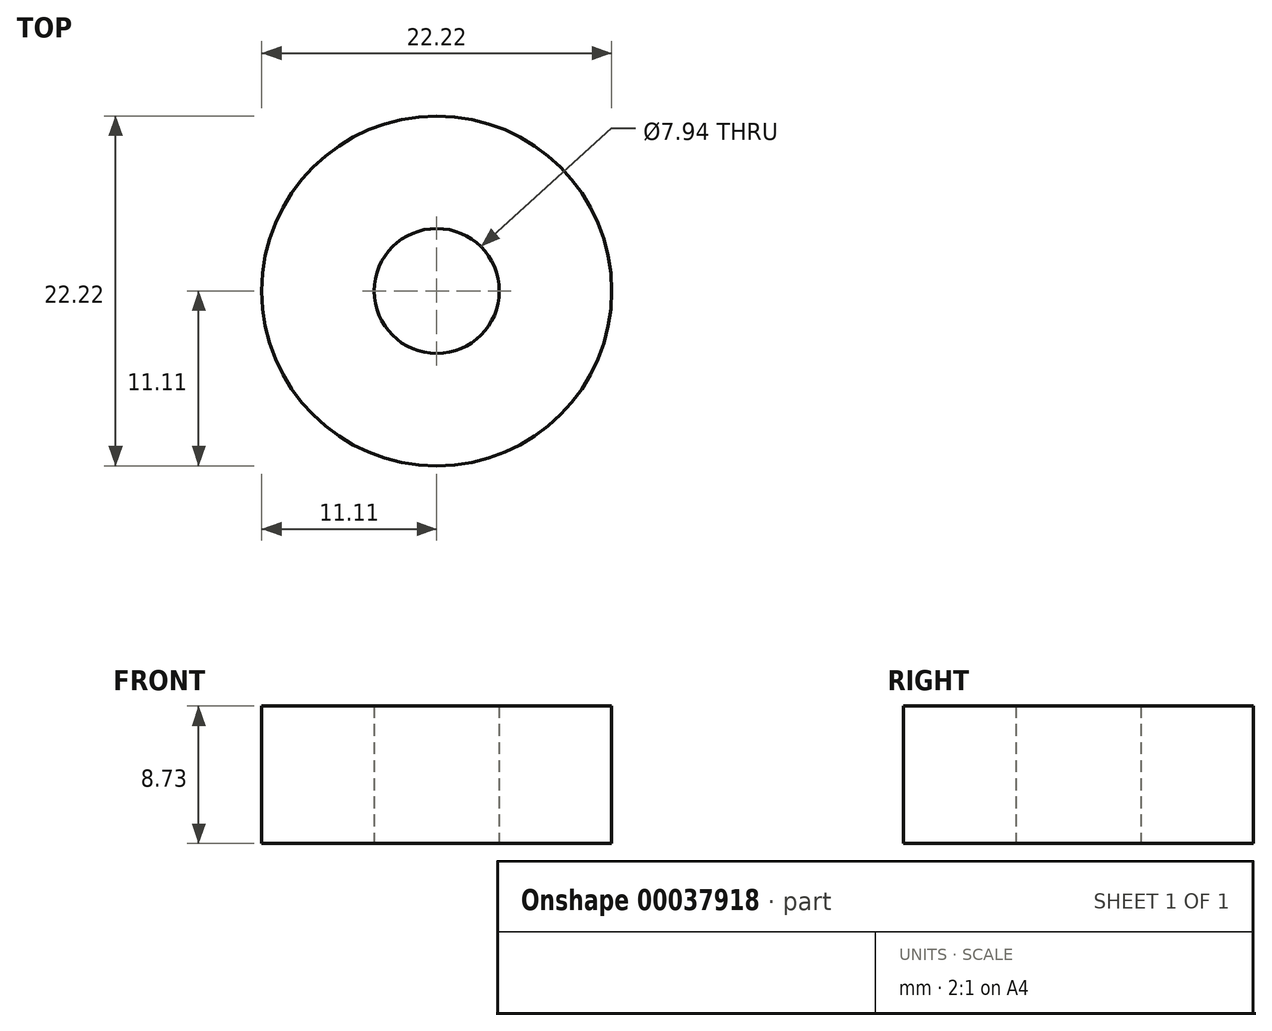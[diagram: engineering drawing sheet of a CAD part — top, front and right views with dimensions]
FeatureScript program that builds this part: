
annotation { "Feature Type Name" : "Feature", "Feature Type Description" : "" }
export const myFeature = defineFeature(function(context is Context, id is Id, definition is map)
    precondition{}
    {
        {
            var Q0;
            Q0=qCreatedBy(makeId("Top.planeOp"),FACE);
            var sketch = newSketch(context, id + "F0", { "sketchPlane" : qUnion([Q0])});
            skCircle(sketch, "E0", {"center": v(0, 0) * mm, "radius": 3.97 * mm});
            skCircle(sketch, "E1", {"center": v(0, 0) * mm, "radius": 11.11 * mm});
            skSolve(sketch);
        }
        {
            var Q0;
            Q0 = qSketchRegion(id + "F0", true);
            extrude(context, id + "F1", {"entities" : qUnion([Q0]), "depth" : 8.73 * mm});
        }
    });
